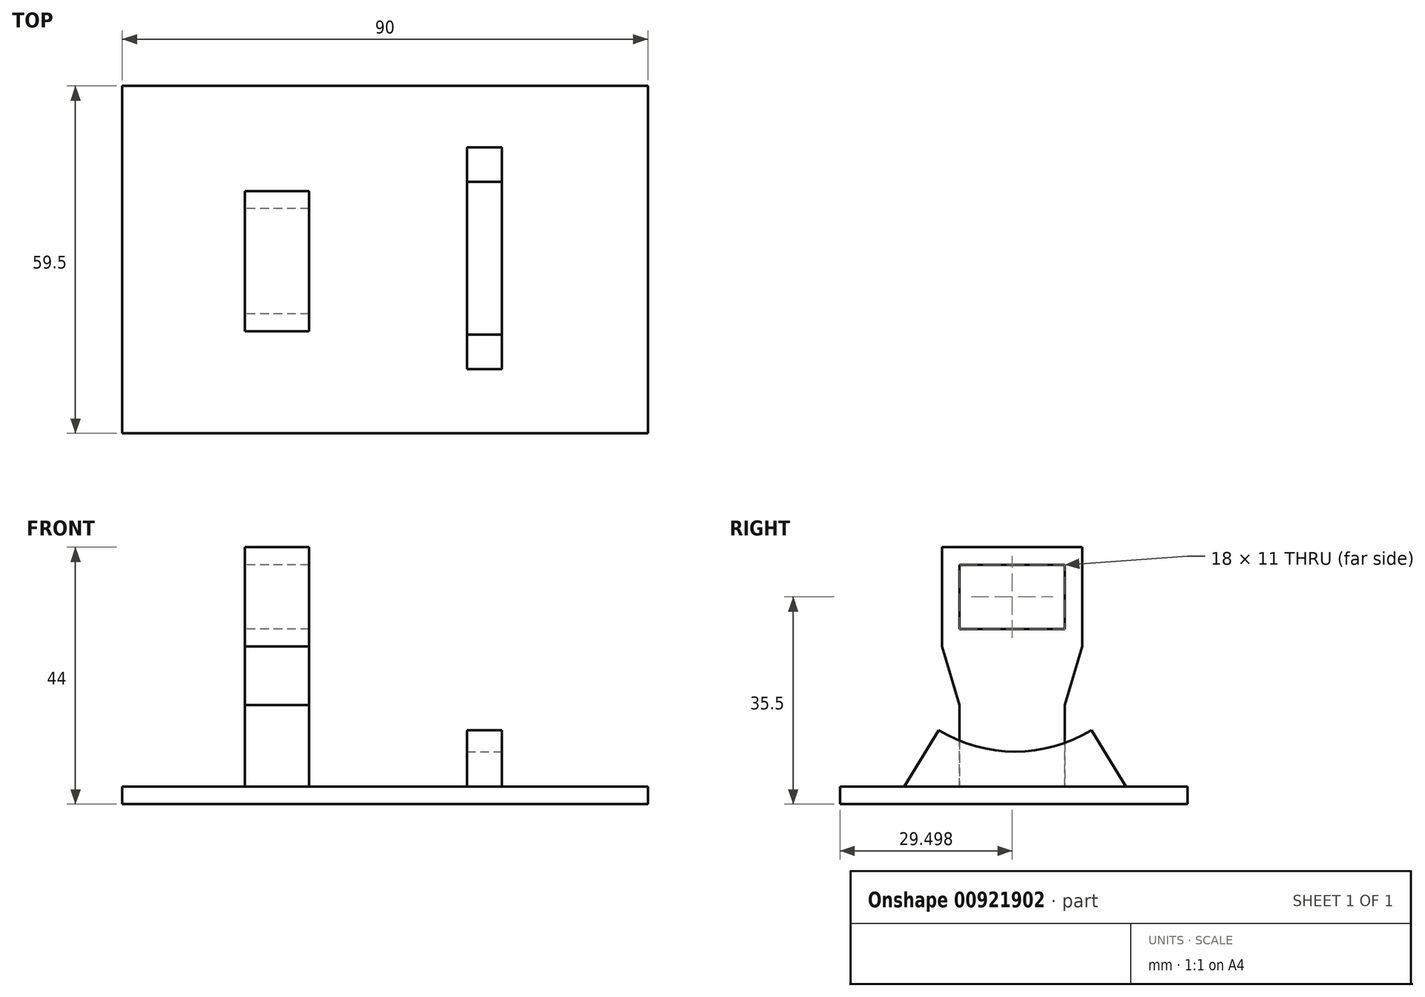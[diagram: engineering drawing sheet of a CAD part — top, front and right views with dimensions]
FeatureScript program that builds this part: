
annotation { "Feature Type Name" : "Feature", "Feature Type Description" : "" }
export const myFeature = defineFeature(function(context is Context, id is Id, definition is map)
    precondition{}
    {
        {
            var Q0;
            Q0=qCreatedBy(makeId("Top.planeOp"),FACE);
            var sketch = newSketch(context, id + "F0", { "sketchPlane" : qUnion([Q0])});
            skLineSegment(sketch, "E0.bottom", {"start": v(0, -0.35) * mm, "end": v(90, -0.35) * mm});
            skLineSegment(sketch, "E0.top", {"start": v(0, 59.15) * mm, "end": v(90, 59.15) * mm});
            skLineSegment(sketch, "E0.left", {"start": v(0, -0.35) * mm, "end": v(0, 59.15) * mm});
            skLineSegment(sketch, "E0.right", {"start": v(90, -0.35) * mm, "end": v(90, 59.15) * mm});
            skSolve(sketch);
        }
        {
            var Q0;
            Q0=makeQuery(id+"F0.imprint","IMPRINT",FACE,{"disambiguationData":[TD([[makeQuery(id+"F0.imprint","IMPRINT",EDGE,{"derivedFrom":sQuery(id+"F0.wireOp",EDGE,"E0.bottom")}),1.0]])]});
            extrude(context, id + "F1", {"entities" : qUnion([Q0]), "depth" : 3 * mm, "offsetDistance" : 25 * mm});
        }
        {
            var Q0;
            Q0=makeQuery(id+"F1.opExtrude","CAP_FACE",FACE,{"disambiguationData":[OSD([sQuery(id+"F0.wireOp",EDGE,"E0.bottom"),sQuery(id+"F0.wireOp",EDGE,"E0.top"),sQuery(id+"F0.wireOp",EDGE,"E0.left"),sQuery(id+"F0.wireOp",EDGE,"E0.right")])],"isStart":false});
            var sketch = newSketch(context, id + "F2", { "sketchPlane" : qUnion([Q0])});
            skLineSegment(sketch, "E1.bottom", {"start": v(21, 41.15) * mm, "end": v(32, 41.15) * mm});
            skLineSegment(sketch, "E1.top", {"start": v(21, 17.15) * mm, "end": v(32, 17.15) * mm});
            skLineSegment(sketch, "E1.left", {"start": v(21, 41.15) * mm, "end": v(21, 17.15) * mm});
            skLineSegment(sketch, "E1.right", {"start": v(32, 41.15) * mm, "end": v(32, 17.15) * mm});
            skLineSegment(sketch, "E2.bottom", {"start": v(59, 57.65) * mm, "end": v(65, 57.65) * mm});
            skLineSegment(sketch, "E2.top", {"start": v(59, 1.65) * mm, "end": v(65, 1.65) * mm});
            skLineSegment(sketch, "E2.left", {"start": v(59, 57.65) * mm, "end": v(59, 1.65) * mm});
            skLineSegment(sketch, "E2.right", {"start": v(65, 57.65) * mm, "end": v(65, 1.65) * mm});
            skSolve(sketch);
        }
        {
            var Q0;
            Q0=makeQuery(id+"F2.imprint","IMPRINT",FACE,{"disambiguationData":[TD([[makeQuery(id+"F2.imprint","IMPRINT",EDGE,{"derivedFrom":sQuery(id+"F2.wireOp",EDGE,"E1.bottom")}),-1.0]])]});
            extrude(context, id + "F3", {"entities" : qUnion([Q0]), "operationType" : NewBodyOperationType.ADD, "depth" : 41 * mm, "offsetDistance" : 25 * mm});
        }
        {
            var Q0;
            Q0=makeQuery(id+"F2.imprint","IMPRINT",FACE,{"disambiguationData":[TD([[makeQuery(id+"F2.imprint","IMPRINT",EDGE,{"derivedFrom":sQuery(id+"F2.wireOp",EDGE,"E2.bottom")}),-1.0]])]});
            extrude(context, id + "F4", {"entities" : qUnion([Q0]), "operationType" : NewBodyOperationType.ADD, "depth" : 31 * mm, "offsetDistance" : 25 * mm});
        }
        {
            var Q0;
            Q0=makeQuery(id+"F3.opExtrude","SWEPT_FACE",FACE,{"disambiguationData":[OSD([sQuery(id+"F2.wireOp",EDGE,"E1.left")])]});
            var sketch = newSketch(context, id + "F5", { "sketchPlane" : qUnion([Q0])});
            skLineSegment(sketch, "E3.bottom", {"start": v(-38.15, 41) * mm, "end": v(-20.15, 41) * mm});
            skLineSegment(sketch, "E3.top", {"start": v(-38.15, 30) * mm, "end": v(-20.15, 30) * mm});
            skLineSegment(sketch, "E3.left", {"start": v(-38.15, 41) * mm, "end": v(-38.15, 30) * mm});
            skLineSegment(sketch, "E3.right", {"start": v(-20.15, 41) * mm, "end": v(-20.15, 30) * mm});
            skLineSegment(sketch, "E4.bottom", {"start": v(-41.15, 3) * mm, "end": v(-38.15, 3) * mm});
            skLineSegment(sketch, "E4.top", {"start": v(-41.15, 27) * mm, "end": v(-38.15, 27) * mm});
            skLineSegment(sketch, "E4.left", {"start": v(-41.15, 3) * mm, "end": v(-41.15, 27) * mm});
            skLineSegment(sketch, "E4.right", {"start": v(-38.15, 3) * mm, "end": v(-38.15, 27) * mm});
            skLineSegment(sketch, "E5.bottom", {"start": v(-17.15, 3) * mm, "end": v(-20.15, 3) * mm});
            skLineSegment(sketch, "E5.top", {"start": v(-17.15, 27) * mm, "end": v(-20.15, 27) * mm});
            skLineSegment(sketch, "E5.left", {"start": v(-17.15, 3) * mm, "end": v(-17.15, 27) * mm});
            skLineSegment(sketch, "E5.right", {"start": v(-20.15, 3) * mm, "end": v(-20.15, 27) * mm});
            skLineSegment(sketch, "E6", {"start": v(-17.15, 27) * mm, "end": v(-20.15, 17) * mm});
            skLineSegment(sketch, "E7", {"start": v(-41.15, 27) * mm, "end": v(-38.15, 17) * mm});
            skSolve(sketch);
        }
        {
            var Q0;
            Q0=makeQuery(id+"F5.imprint","IMPRINT",FACE,{"disambiguationData":[TD([[makeQuery(id+"F5.imprint","IMPRINT",EDGE,{"derivedFrom":sQuery(id+"F5.wireOp",EDGE,"E4.bottom")}),1.0]])]});
            var Q1;
            Q1=makeQuery(id+"F5.imprint","IMPRINT",FACE,{"disambiguationData":[TD([[makeQuery(id+"F5.imprint","IMPRINT",EDGE,{"derivedFrom":sQuery(id+"F5.wireOp",EDGE,"E3.bottom")}),-1.0]])]});
            var Q2;
            Q2=makeQuery(id+"F5.imprint","IMPRINT",FACE,{"disambiguationData":[TD([[makeQuery(id+"F5.imprint","IMPRINT",EDGE,{"derivedFrom":sQuery(id+"F5.wireOp",EDGE,"E5.bottom")}),1.0]])]});
            extrude(context, id + "F6", {"entities" : qUnion([Q0, Q1, Q2]), "operationType" : NewBodyOperationType.REMOVE, "oppositeDirection" : true, "depth" : 15 * mm, "offsetDistance" : 25 * mm});
        }
        {
            var Q0;
            Q0=makeQuery(id+"F4.opExtrude","SWEPT_FACE",FACE,{"disambiguationData":[OSD([sQuery(id+"F2.wireOp",EDGE,"E2.right")])]});
            var sketch = newSketch(context, id + "F7", { "sketchPlane" : qUnion([Q0])});
            skCircle(sketch, "E8", {"center": v(29.65, 34) * mm, "radius": 25 * mm});
            skCircle(sketch, "E9", {"center": v(29.65, 34) * mm, "radius": 28 * mm});
            skLineSegment(sketch, "E10", {"start": v(25.65, 6.29) * mm, "end": v(25.65, 3) * mm});
            skLineSegment(sketch, "E11", {"start": v(33.65, 6.29) * mm, "end": v(33.65, 3) * mm});
            skLineSegment(sketch, "E12", {"start": v(29.65, 34) * mm, "end": v(48.65, 3) * mm});
            skLineSegment(sketch, "E13", {"start": v(29.65, 34) * mm, "end": v(10.65, 3) * mm});
            skSolve(sketch);
        }
        {
            var Q0;
            {var subQ0=sQuery(id+"F7.wireOp",EDGE,"E13");var subQ1=sQuery(id+"F7.wireOp",EDGE,"E8");var subQ2=makeQuery(id+"F7.imprint","INTERSECT",VERTEX,{"derivedFrom":[subQ1,subQ0]});Q0=makeQuery(id+"F7.imprint","IMPRINT",FACE,{"disambiguationData":[TD([[makeQuery(id+"F7.imprint","IMPRINT",EDGE,{"disambiguationData":[TD([[subQ2,1.0]])],"derivedFrom":subQ1}),1.0]])]});}
            var Q1;
            {var subQ0=sQuery(id+"F7.wireOp",EDGE,"E13");var subQ1=sQuery(id+"F7.wireOp",EDGE,"E8");var subQ2=makeQuery(id+"F7.imprint","INTERSECT",VERTEX,{"derivedFrom":[subQ1,subQ0]});Q1=makeQuery(id+"F7.imprint","IMPRINT",FACE,{"disambiguationData":[TD([[makeQuery(id+"F7.imprint","IMPRINT",EDGE,{"disambiguationData":[TD([[subQ2,-1.0]])],"derivedFrom":subQ1}),1.0]])]});}
            var Q2;
            {var subQ0=sQuery(id+"F7.wireOp",EDGE,"E12");var subQ1=sQuery(id+"F7.wireOp",EDGE,"E8");var subQ2=makeQuery(id+"F7.imprint","INTERSECT",VERTEX,{"derivedFrom":[subQ1,subQ0]});Q2=makeQuery(id+"F7.imprint","IMPRINT",FACE,{"disambiguationData":[TD([[makeQuery(id+"F7.imprint","IMPRINT",EDGE,{"disambiguationData":[TD([[subQ2,-1.0]])],"derivedFrom":subQ1}),1.0]])]});}
            var Q3;
            {var subQ0=sQuery(id+"F7.wireOp",EDGE,"E13");var subQ1=sQuery(id+"F7.wireOp",EDGE,"E8");var subQ2=makeQuery(id+"F7.imprint","INTERSECT",VERTEX,{"derivedFrom":[subQ1,subQ0]});Q3=makeQuery(id+"F7.imprint","IMPRINT",FACE,{"disambiguationData":[TD([[makeQuery(id+"F7.imprint","IMPRINT",EDGE,{"disambiguationData":[TD([[subQ2,1.0]])],"derivedFrom":subQ1}),-1.0]])]});}
            var Q4;
            {var subQ1=sQuery(id+"F2.wireOp",EDGE,"E2.right");var subQ2=makeQuery(id+"F4.opExtrude","SWEPT_EDGE",EDGE,{"disambiguationData":[OSD([sQuery(id+"F2.wireOp",EDGE,"E2.top"),subQ1])]});Q4=makeQuery(id+"F7.imprint","IMPRINT",FACE,{"disambiguationData":[TD([[makeQuery(id+"F7.imprint","IMPRINT",EDGE,{"derivedFrom":subQ2}),1.0]])]});}
            var Q5;
            {var subQ1=sQuery(id+"F2.wireOp",EDGE,"E2.right");var subQ2=makeQuery(id+"F4.opExtrude","SWEPT_EDGE",EDGE,{"disambiguationData":[OSD([sQuery(id+"F2.wireOp",EDGE,"E2.bottom"),subQ1])]});Q5=makeQuery(id+"F7.imprint","IMPRINT",FACE,{"disambiguationData":[TD([[makeQuery(id+"F7.imprint","IMPRINT",EDGE,{"derivedFrom":subQ2}),-1.0]])]});}
            var Q6;
            {var subQ0=sQuery(id+"F7.wireOp",EDGE,"E12");var subQ1=sQuery(id+"F7.wireOp",EDGE,"E8");var subQ2=makeQuery(id+"F7.imprint","INTERSECT",VERTEX,{"derivedFrom":[subQ1,subQ0]});Q6=makeQuery(id+"F7.imprint","IMPRINT",FACE,{"disambiguationData":[TD([[makeQuery(id+"F7.imprint","IMPRINT",EDGE,{"disambiguationData":[TD([[subQ2,-1.0]])],"derivedFrom":subQ1}),-1.0]])]});}
            extrude(context, id + "F8", {"entities" : qUnion([Q0, Q1, Q2, Q3, Q4, Q5, Q6]), "operationType" : NewBodyOperationType.REMOVE, "oppositeDirection" : true, "depth" : 10 * mm, "offsetDistance" : 25 * mm});
        }
    });
